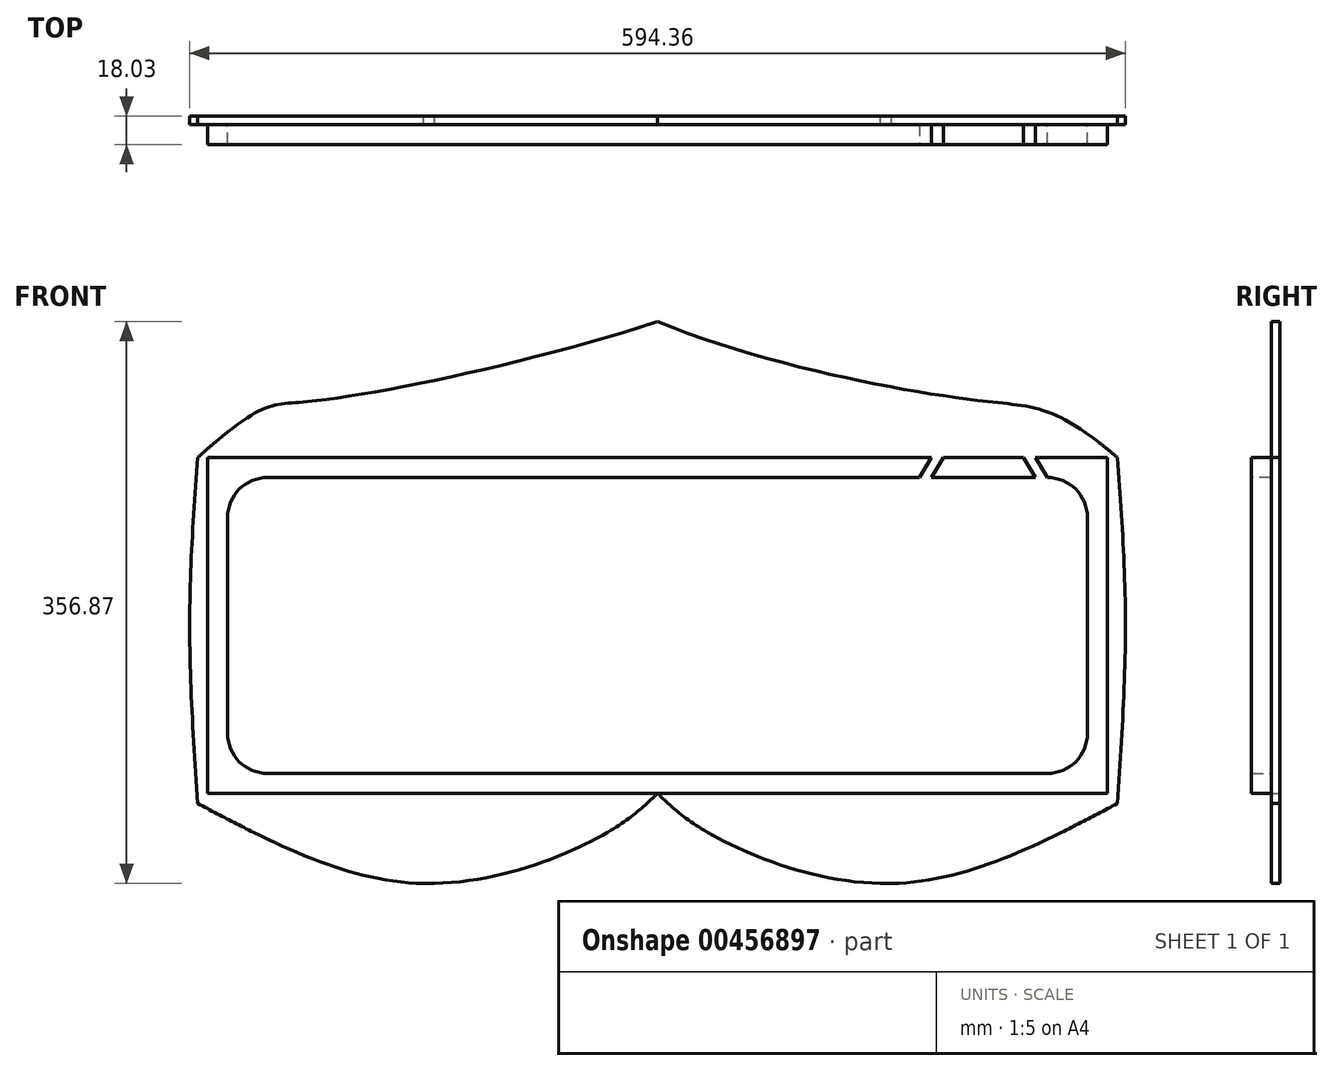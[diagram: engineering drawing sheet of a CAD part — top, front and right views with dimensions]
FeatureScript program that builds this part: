
annotation { "Feature Type Name" : "Feature", "Feature Type Description" : "" }
export const myFeature = defineFeature(function(context is Context, id is Id, definition is map)
    precondition{}
    {
        {
            var Q0;
            Q0=qCreatedBy(makeId("Front.planeOp"),FACE);
            var sketch = newSketch(context, id + "F0", { "sketchPlane" : qUnion([Q0])});
            skLineSegment(sketch, "E0.bottom", {"start": v(0, 0) * mm, "end": v(-584.2, 0) * mm});
            skLineSegment(sketch, "E0.top", {"start": v(0, 219.7) * mm, "end": v(-584.2, 219.7) * mm});
            skLineSegment(sketch, "E0.left", {"start": v(0, 0) * mm, "end": v(0, 219.7) * mm});
            skLineSegment(sketch, "E0.right", {"start": v(-584.2, 0) * mm, "end": v(-584.2, 219.7) * mm});
            skPoint(sketch, "E1", {"position": v(-292.1, 219.7) * mm});
            skSolve(sketch);
        }
        {
            var Q0;
            Q0=makeQuery(id+"F0.imprint","IMPRINT",FACE,{"disambiguationData":[TD([[makeQuery(id+"F0.imprint","IMPRINT",EDGE,{"derivedFrom":sQuery(id+"F0.wireOp",EDGE,"E0.bottom")}),-1.0]])]});
            extrude(context, id + "F1", {"entities" : qUnion([Q0]), "depth" : 5.33 * mm});
        }
        {
            var Q0;
            Q0=makeQuery(id+"F1.opExtrude","CAP_FACE",FACE,{"disambiguationData":[OSD([sQuery(id+"F0.wireOp",EDGE,"E0.bottom"),sQuery(id+"F0.wireOp",EDGE,"E0.top"),sQuery(id+"F0.wireOp",EDGE,"E0.left"),sQuery(id+"F0.wireOp",EDGE,"E0.right")])],"isStart":false});
            var sketch = newSketch(context, id + "F2", { "sketchPlane" : qUnion([Q0])});
            skLineSegment(sketch, "E2", {"start": v(-577.85, 219.7) * mm, "end": v(-577.85, 6.35) * mm});
            skLineSegment(sketch, "E3", {"start": v(-577.85, 6.35) * mm, "end": v(-6.35, 6.35) * mm});
            skLineSegment(sketch, "E4", {"start": v(-6.35, 6.35) * mm, "end": v(-6.35, 219.71) * mm});
            skLineSegment(sketch, "E5", {"start": v(-6.35, 219.71) * mm, "end": v(-577.85, 219.7) * mm});
            skLineSegment(sketch, "E6", {"start": v(-565.15, 207) * mm, "end": v(-565.15, 19.05) * mm});
            skLineSegment(sketch, "E7", {"start": v(-565.15, 19.05) * mm, "end": v(-19.05, 19.05) * mm});
            skLineSegment(sketch, "E8", {"start": v(-19.05, 19.05) * mm, "end": v(-19.05, 207.01) * mm});
            skLineSegment(sketch, "E9", {"start": v(-19.05, 207.01) * mm, "end": v(-565.15, 207) * mm});
            skSolve(sketch);
        }
        {
            var Q0;
            Q0=makeQuery(id+"F2.imprint","IMPRINT",FACE,{"disambiguationData":[TD([[makeQuery(id+"F2.imprint","IMPRINT",EDGE,{"derivedFrom":sQuery(id+"F2.wireOp",EDGE,"E2")}),1.0]])]});
            extrude(context, id + "F3", {"entities" : qUnion([Q0]), "operationType" : NewBodyOperationType.ADD, "depth" : 12.7 * mm});
        }
        {
            var Q0;
            Q0=makeQuery(id+"F3.opExtrude","SWEPT_EDGE",EDGE,{"disambiguationData":[OSD([sQuery(id+"F2.wireOp",EDGE,"E6"),sQuery(id+"F2.wireOp",EDGE,"E9")])]});
            var Q1;
            Q1=makeQuery(id+"F3.opExtrude","SWEPT_EDGE",EDGE,{"disambiguationData":[OSD([sQuery(id+"F2.wireOp",EDGE,"E8"),sQuery(id+"F2.wireOp",EDGE,"E9")])]});
            var Q2;
            Q2=makeQuery(id+"F3.opExtrude","SWEPT_EDGE",EDGE,{"disambiguationData":[OSD([sQuery(id+"F2.wireOp",EDGE,"E7"),sQuery(id+"F2.wireOp",EDGE,"E8")])]});
            var Q3;
            Q3=makeQuery(id+"F3.opExtrude","SWEPT_EDGE",EDGE,{"disambiguationData":[OSD([sQuery(id+"F2.wireOp",EDGE,"E6"),sQuery(id+"F2.wireOp",EDGE,"E7")])]});
            fillet(context, id + "F4", {"entities" : qUnion([Q0, Q1, Q2, Q3]), "radius" : 25.4 * mm, "tangentPropagation" : true, "allowEdgeOverflow" : false});
        }
        {
            var Q0;
            Q0=makeQuery(id+"F3.opExtrude","CAP_FACE",FACE,{"disambiguationData":[OSD([sQuery(id+"F2.wireOp",EDGE,"E2"),sQuery(id+"F2.wireOp",EDGE,"E3"),sQuery(id+"F2.wireOp",EDGE,"E4"),sQuery(id+"F2.wireOp",EDGE,"E5"),sQuery(id+"F2.wireOp",EDGE,"E6"),sQuery(id+"F2.wireOp",EDGE,"E7"),sQuery(id+"F2.wireOp",EDGE,"E8"),sQuery(id+"F2.wireOp",EDGE,"E9")])],"isStart":false});
            var sketch = newSketch(context, id + "F5", { "sketchPlane" : qUnion([Q0])});
            skPoint(sketch, "E10", {"position": v(-118.11, 219.7) * mm});
            skPoint(sketch, "E11", {"position": v(-110.5, 219.7) * mm});
            skPoint(sketch, "E12", {"position": v(-59.69, 219.7) * mm});
            skPoint(sketch, "E13", {"position": v(-52.07, 219.7) * mm});
            skPoint(sketch, "E14", {"position": v(-376.28, 272.75) * mm});
            skPoint(sketch, "E15", {"position": v(-12.7, 0) * mm});
            skPoint(sketch, "E16", {"position": v(-20.32, 0) * mm});
            skLineSegment(sketch, "E17", {"start": v(-20.32, 0) * mm, "end": v(-12.7, 0) * mm});
            skPoint(sketch, "E18", {"position": v(-118.11, 207.01) * mm});
            skPoint(sketch, "E19", {"position": v(-125.73, 207.01) * mm});
            skLineSegment(sketch, "E20", {"start": v(-125.73, 207.01) * mm, "end": v(-118.11, 219.7) * mm});
            skLineSegment(sketch, "E21", {"start": v(-125.73, 207.01) * mm, "end": v(-118.11, 207.01) * mm});
            skLineSegment(sketch, "E22", {"start": v(-118.11, 207.01) * mm, "end": v(-110.5, 219.7) * mm});
            skLineSegment(sketch, "E23", {"start": v(-118.11, 219.7) * mm, "end": v(-110.5, 219.7) * mm});
            skLineSegment(sketch, "E24", {"start": v(-59.69, 219.7) * mm, "end": v(-52.07, 219.7) * mm});
            skLineSegment(sketch, "E25", {"start": v(-110.5, 219.7) * mm, "end": v(-59.69, 219.7) * mm});
            skLineSegment(sketch, "E26", {"start": v(-59.69, 219.7) * mm, "end": v(-110.5, 219.7) * mm});
            skLineSegment(sketch, "E27", {"start": v(-110.5, 219.7) * mm, "end": v(-113.58, 214.56) * mm});
            skPoint(sketch, "E28", {"position": v(-44.45, 207.01) * mm});
            skPoint(sketch, "E29", {"position": v(-52.07, 207.01) * mm});
            skLineSegment(sketch, "E30", {"start": v(-59.69, 219.7) * mm, "end": v(-52.07, 207.01) * mm});
            skLineSegment(sketch, "E31", {"start": v(-52.07, 219.7) * mm, "end": v(-44.45, 207.01) * mm});
            skLineSegment(sketch, "E32", {"start": v(-52.07, 207.01) * mm, "end": v(-44.45, 207.01) * mm});
            skLineSegment(sketch, "E33", {"start": v(-52.07, 219.7) * mm, "end": v(-59.69, 219.7) * mm});
            skPoint(sketch, "E34", {"position": v(-56.6, 214.56) * mm});
            skLineSegment(sketch, "E35", {"start": v(-113.58, 214.56) * mm, "end": v(-56.6, 214.56) * mm});
            skSolve(sketch);
        }
        {
            var Q0;
            Q0=makeQuery(id+"F5.imprint","IMPRINT",FACE,{"disambiguationData":[TD([[makeQuery(id+"F5.imprint","IMPRINT",EDGE,{"derivedFrom":sQuery(id+"F5.wireOp",EDGE,"E20")}),-1.0]])]});
            var Q1;
            {var subQ8=sQuery(id+"F5.wireOp",EDGE,"RZINdJYM-ykuw-GilU-JIjt-DnibDYUsXZuo");Q1=makeQuery(id+"F5.imprint","IMPRINT",FACE,{"disambiguationData":[TD([[makeQuery(id+"F5.imprint","IMPRINT",EDGE,{"derivedFrom":subQ8}),1.0]])]});}
            var Q2;
            Q2=makeQuery(id+"F5.imprint","IMPRINT",FACE,{"disambiguationData":[TD([[makeQuery(id+"F5.imprint","IMPRINT",EDGE,{"derivedFrom":sQuery(id+"F5.wireOp",EDGE,"RZINdJYM-ykuw-GilU-JIjt-DnibDYUsXZuo")}),-1.0]])]});
            var Q3;
            Q3=makeQuery(id+"F5.imprint","IMPRINT",FACE,{"disambiguationData":[TD([[makeQuery(id+"F5.imprint","IMPRINT",EDGE,{"derivedFrom":sQuery(id+"F5.wireOp",EDGE,"NQJIxGkc-Vixr-o2zM-VUe3-bVQ5EoZFKsab")}),1.0]])]});
            var Q4;
            Q4=makeQuery(id+"F5.imprint","IMPRINT",FACE,{"disambiguationData":[TD([[makeQuery(id+"F5.imprint","IMPRINT",EDGE,{"derivedFrom":sQuery(id+"F5.wireOp",EDGE,"E30")}),1.0]])]});
            var Q5;
            {var subQ0=sQuery(id+"F5.wireOp",EDGE,"E26");Q5=makeQuery(id+"F5.imprint","IMPRINT",FACE,{"disambiguationData":[TD([[makeQuery(id+"F5.imprint","IMPRINT",EDGE,{"derivedFrom":subQ0}),1.0]])]});}
            extrude(context, id + "F6", {"entities" : qUnion([Q0, Q1, Q2, Q3, Q4, Q5]), "operationType" : NewBodyOperationType.REMOVE, "oppositeDirection" : true, "depth" : 12.7 * mm});
        }
        {
            var Q0;
            Q0=makeQuery(id+"F1.opExtrude","CAP_FACE",FACE,{"disambiguationData":[OSD([sQuery(id+"F0.wireOp",EDGE,"E0.bottom"),sQuery(id+"F0.wireOp",EDGE,"E0.top"),sQuery(id+"F0.wireOp",EDGE,"E0.left"),sQuery(id+"F0.wireOp",EDGE,"E0.right")])],"isStart":true});
            var sketch = newSketch(context, id + "F7", { "sketchPlane" : qUnion([Q0])});
            skLineSegment(sketch, "E36", {"start": v(0, 0) * mm, "end": v(-5.08, 0) * mm});
            skLineSegment(sketch, "E37", {"start": v(-5.08, 0) * mm, "end": v(-5.08, 229.87) * mm});
            skLineSegment(sketch, "E38", {"start": v(-5.08, 229.87) * mm, "end": v(589.28, 229.87) * mm});
            skLineSegment(sketch, "E39", {"start": v(589.28, 229.87) * mm, "end": v(589.28, 0) * mm});
            skLineSegment(sketch, "E40", {"start": v(589.28, 0) * mm, "end": v(584.2, 0) * mm});
            skPoint(sketch, "E41", {"position": v(589.28, 114.93) * mm});
            skPoint(sketch, "E42", {"position": v(584.2, 109.85) * mm});
            skPoint(sketch, "E43", {"position": v(292.1, 229.87) * mm});
            skPoint(sketch, "E44", {"position": v(292.1, 219.7) * mm});
            skPoint(sketch, "E45", {"position": v(-5.08, 114.93) * mm});
            skPoint(sketch, "E46", {"position": v(0, 109.85) * mm});
            skPoint(sketch, "E47", {"position": v(538.48, 229.87) * mm});
            skPoint(sketch, "E48", {"position": v(45.72, 229.87) * mm});
            skPoint(sketch, "E49", {"position": v(-5.08, 191.77) * mm});
            skPoint(sketch, "E50", {"position": v(589.28, 191.77) * mm});
            skPoint(sketch, "E51", {"position": v(584.2, 183.25) * mm});
            skPoint(sketch, "E52", {"position": v(0, 176.13) * mm});
            skPoint(sketch, "E53", {"position": v(589.28, 63.5) * mm});
            skPoint(sketch, "E54", {"position": v(-5.08, 63.5) * mm});
            skPoint(sketch, "E55", {"position": v(0, 219.7) * mm});
            skPoint(sketch, "E56", {"position": v(584.2, 219.7) * mm});
            skPoint(sketch, "E57", {"position": v(393.7, 219.7) * mm});
            skPoint(sketch, "E58", {"position": v(190.5, 219.7) * mm});
            skLineSegment(sketch, "E59", {"start": v(292.1, 219.7) * mm, "end": v(-5.08, 229.87) * mm});
            skLineSegment(sketch, "E60", {"start": v(292.1, 219.7) * mm, "end": v(589.28, 229.87) * mm});
            skLineSegment(sketch, "E61", {"start": v(589.28, -18.42) * mm, "end": v(-5.08, -18.42) * mm});
            skLineSegment(sketch, "E62", {"start": v(589.28, 0) * mm, "end": v(589.28, -18.42) * mm});
            skLineSegment(sketch, "E63", {"start": v(292.1, 229.87) * mm, "end": v(292.1, 306.07) * mm});
            skPoint(sketch, "E64", {"position": v(292.1, -18.42) * mm});
            skLineSegment(sketch, "E65", {"start": v(589.28, -18.42) * mm, "end": v(589.28, -50.8) * mm});
            skLineSegment(sketch, "E66", {"start": v(589.28, -50.8) * mm, "end": v(292.1, -50.8) * mm});
            skPoint(sketch, "E67", {"position": v(292.1, 0) * mm});
            skPoint(sketch, "E68", {"position": v(440.69, -50.8) * mm});
            skLineSegment(sketch, "E69", {"start": v(292.1, -50.8) * mm, "end": v(-4.91, -50.8) * mm});
            skLineSegment(sketch, "E70", {"start": v(-4.91, -50.8) * mm, "end": v(-5.08, -18.42) * mm});
            skPoint(sketch, "E71", {"position": v(143.6, -50.8) * mm});
            skPoint(sketch, "E72", {"position": v(551.18, -18.42) * mm});
            skPoint(sketch, "E73", {"position": v(33.02, -18.42) * mm});
            skPoint(sketch, "E74", {"position": v(6.35, 219.7) * mm});
            skPoint(sketch, "E75", {"position": v(577.85, 219.7) * mm});
            skPoint(sketch, "E76", {"position": v(6.35, 0) * mm});
            skPoint(sketch, "E77", {"position": v(577.85, 0) * mm});
            skPoint(sketch, "E78", {"position": v(82.55, 229.87) * mm});
            skPoint(sketch, "E79", {"position": v(514.35, 229.87) * mm});
            skLineSegment(sketch, "E80", {"start": v(82.55, 229.87) * mm, "end": v(82.55, 255.27) * mm});
            skLineSegment(sketch, "E81", {"start": v(514.35, 229.87) * mm, "end": v(514.35, 255.27) * mm});
            skLineSegment(sketch, "E82", {"start": v(292.1, 0) * mm, "end": v(292.1, 6.35) * mm});
            skPoint(sketch, "E83", {"position": v(323.85, -18.42) * mm});
            skPoint(sketch, "E84", {"position": v(260.35, -18.42) * mm});
            skFitSpline(sketch, "E85", {"points": [v(292.1, 6.35) * mm, v(323.85, -18.42) * mm, v(440.69, -50.8) * mm, v(584.2, 0) * mm], "startDerivative": vector(117.09, -111.78) * mm, "endDerivative": vector(338.96, 179.53) * mm});
            skFitSpline(sketch, "E86", {"points": [v(584.2, 0) * mm, v(589.28, 114.94) * mm, v(584.2, 219.7) * mm], "startDerivative": vector(15.13, 227.29) * mm, "endDerivative": vector(-15.37, 212.01) * mm});
            skFitSpline(sketch, "E87", {"points": [v(0, 0) * mm, v(-5.08, 114.94) * mm, v(0, 219.7) * mm], "startDerivative": vector(-15.13, 227.29) * mm, "endDerivative": vector(15.37, 212.01) * mm});
            skFitSpline(sketch, "E88", {"points": [v(292.1, 6.35) * mm, v(260.35, -18.42) * mm, v(143.6, -50.8) * mm, v(0, 0) * mm], "startDerivative": vector(-117.11, -111.77) * mm, "endDerivative": vector(-339.14, 179.5) * mm});
            skFitSpline(sketch, "E89", {"points": [v(292.1, 306.07) * mm, v(514.35, 255.27) * mm, v(584.2, 219.7) * mm], "startDerivative": vector(389.1, -127.04) * mm, "endDerivative": vector(333.85, -297.61) * mm});
            skFitSpline(sketch, "E90", {"points": [v(292.1, 306.07) * mm, v(82.55, 255.27) * mm, v(0, 219.7) * mm], "startDerivative": vector(-362.71, -146.77) * mm, "endDerivative": vector(-299.5, -254.41) * mm});
            skSolve(sketch);
        }
        {
            var Q0;
            {var subQ0=sQuery(id+"F7.wireOp",EDGE,"E82");Q0=makeQuery(id+"F7.imprint","IMPRINT",FACE,{"disambiguationData":[TD([[makeQuery(id+"F7.imprint","IMPRINT",EDGE,{"derivedFrom":subQ0}),1.0]])]});}
            var Q1;
            {var subQ0=sQuery(id+"F7.wireOp",EDGE,"E82");Q1=makeQuery(id+"F7.imprint","IMPRINT",FACE,{"disambiguationData":[TD([[makeQuery(id+"F7.imprint","IMPRINT",EDGE,{"derivedFrom":subQ0}),-1.0]])]});}
            extrude(context, id + "F8", {"entities" : qUnion([Q0, Q1]), "operationType" : NewBodyOperationType.REMOVE, "depth" : -5.33 * mm});
        }
        {
            var Q0;
            {var subQ0=sQuery(id+"F7.wireOp",EDGE,"E80");Q0=makeQuery(id+"F7.imprint","IMPRINT",FACE,{"disambiguationData":[TD([[makeQuery(id+"F7.imprint","IMPRINT",EDGE,{"derivedFrom":subQ0}),1.0]])]});}
            var Q1;
            {var subQ0=sQuery(id+"F7.wireOp",EDGE,"E63");Q1=makeQuery(id+"F7.imprint","IMPRINT",FACE,{"disambiguationData":[TD([[makeQuery(id+"F7.imprint","IMPRINT",EDGE,{"derivedFrom":subQ0}),1.0]])]});}
            var Q2;
            {var subQ0=sQuery(id+"F7.wireOp",EDGE,"E63");Q2=makeQuery(id+"F7.imprint","IMPRINT",FACE,{"disambiguationData":[TD([[makeQuery(id+"F7.imprint","IMPRINT",EDGE,{"derivedFrom":subQ0}),-1.0]])]});}
            var Q3;
            {var subQ0=sQuery(id+"F7.wireOp",EDGE,"E81");Q3=makeQuery(id+"F7.imprint","IMPRINT",FACE,{"disambiguationData":[TD([[makeQuery(id+"F7.imprint","IMPRINT",EDGE,{"derivedFrom":subQ0}),-1.0]])]});}
            var Q4;
            {var subQ0=sQuery(id+"F7.wireOp",EDGE,"E60");var subQ3=sQuery(id+"F7.wireOp",EDGE,"c924a81b-7c33-454b-bec7-e8dcdf9a45a6");var subQ4=makeQuery(id+"F7.imprint","INTERSECT",VERTEX,{"derivedFrom":[subQ0,subQ3]});Q4=makeQuery(id+"F7.imprint","IMPRINT",FACE,{"disambiguationData":[TD([[makeQuery(id+"F7.imprint","IMPRINT",EDGE,{"disambiguationData":[TD([[subQ4,1.0]])],"derivedFrom":subQ0}),-1.0]])]});}
            var Q5;
            {var subQ0=sQuery(id+"F7.wireOp",EDGE,"E38");var subQ7=makeQuery(id+"F7.imprint","INTERSECT",VERTEX,{"derivedFrom":[subQ0,sQuery(id+"F7.wireOp",EDGE,"E80")]});Q5=makeQuery(id+"F7.imprint","IMPRINT",FACE,{"disambiguationData":[TD([[makeQuery(id+"F7.imprint","IMPRINT",EDGE,{"disambiguationData":[TD([[subQ7,1.0]])],"derivedFrom":subQ0}),-1.0]])]});}
            var Q6;
            {var subQ0=sQuery(id+"F7.wireOp",EDGE,"E59");var subQ3=sQuery(id+"F7.wireOp",EDGE,"3c0d3bf1-8729-4a13-bacb-ae9455c1fce2");var subQ4=makeQuery(id+"F7.imprint","INTERSECT",VERTEX,{"derivedFrom":[subQ0,subQ3]});Q6=makeQuery(id+"F7.imprint","IMPRINT",FACE,{"disambiguationData":[TD([[makeQuery(id+"F7.imprint","IMPRINT",EDGE,{"disambiguationData":[TD([[subQ4,1.0]])],"derivedFrom":subQ0}),1.0]])]});}
            var Q7;
            {var subQ0=sQuery(id+"F7.wireOp",EDGE,"c8baf287-04a5-4912-9b82-47411f5b9158");var subQ1=sQuery(id+"F7.wireOp",EDGE,"E61");var subQ2=makeQuery(id+"F7.imprint","INTERSECT",VERTEX,{"disambiguationData":[OD(0.0)],"derivedFrom":[subQ1,subQ0]});Q7=makeQuery(id+"F7.imprint","IMPRINT",FACE,{"disambiguationData":[TD([[makeQuery(id+"F7.imprint","IMPRINT",EDGE,{"disambiguationData":[TD([[subQ2,1.0]])],"derivedFrom":subQ1}),-1.0]])]});}
            var Q8;
            {var subQ0=sQuery(id+"F7.wireOp",EDGE,"c8baf287-04a5-4912-9b82-47411f5b9158");var subQ1=sQuery(id+"F7.wireOp",EDGE,"E61");var subQ2=makeQuery(id+"F7.imprint","INTERSECT",VERTEX,{"disambiguationData":[OD(0.0)],"derivedFrom":[subQ1,subQ0]});Q8=makeQuery(id+"F7.imprint","IMPRINT",FACE,{"disambiguationData":[TD([[makeQuery(id+"F7.imprint","IMPRINT",EDGE,{"disambiguationData":[TD([[subQ2,1.0]])],"derivedFrom":subQ1}),1.0]])]});}
            var Q9;
            {var subQ0=sQuery(id+"F7.wireOp",EDGE,"c47f91c2-344f-4819-b83d-0fa72e82eadb");var subQ1=sQuery(id+"F7.wireOp",EDGE,"E61");var subQ2=makeQuery(id+"F7.imprint","INTERSECT",VERTEX,{"disambiguationData":[OD(0.0)],"derivedFrom":[subQ1,subQ0]});Q9=makeQuery(id+"F7.imprint","IMPRINT",FACE,{"disambiguationData":[TD([[makeQuery(id+"F7.imprint","IMPRINT",EDGE,{"disambiguationData":[TD([[subQ2,-1.0]])],"derivedFrom":subQ1}),-1.0]])]});}
            var Q10;
            {var subQ0=sQuery(id+"F7.wireOp",EDGE,"c47f91c2-344f-4819-b83d-0fa72e82eadb");var subQ1=sQuery(id+"F7.wireOp",EDGE,"E61");var subQ2=makeQuery(id+"F7.imprint","INTERSECT",VERTEX,{"disambiguationData":[OD(0.0)],"derivedFrom":[subQ1,subQ0]});Q10=makeQuery(id+"F7.imprint","IMPRINT",FACE,{"disambiguationData":[TD([[makeQuery(id+"F7.imprint","IMPRINT",EDGE,{"disambiguationData":[TD([[subQ2,-1.0]])],"derivedFrom":subQ1}),1.0]])]});}
            var Q11;
            {var subQ0=sQuery(id+"F7.wireOp",EDGE,"E85");var subQ1=sQuery(id+"F7.wireOp",EDGE,"E61");var subQ2=makeQuery(id+"F7.imprint","INTERSECT",VERTEX,{"disambiguationData":[OD(0.0)],"derivedFrom":[subQ1,subQ0]});Q11=makeQuery(id+"F7.imprint","IMPRINT",FACE,{"disambiguationData":[TD([[makeQuery(id+"F7.imprint","IMPRINT",EDGE,{"disambiguationData":[TD([[subQ2,-1.0]])],"derivedFrom":subQ1}),1.0]])]});}
            var Q12;
            {var subQ0=sQuery(id+"F7.wireOp",EDGE,"E85");var subQ1=sQuery(id+"F7.wireOp",EDGE,"E61");var subQ2=makeQuery(id+"F7.imprint","INTERSECT",VERTEX,{"disambiguationData":[OD(0.0)],"derivedFrom":[subQ1,subQ0]});Q12=makeQuery(id+"F7.imprint","IMPRINT",FACE,{"disambiguationData":[TD([[makeQuery(id+"F7.imprint","IMPRINT",EDGE,{"disambiguationData":[TD([[subQ2,-1.0]])],"derivedFrom":subQ1}),-1.0]])]});}
            var Q13;
            {var subQ0=sQuery(id+"F7.wireOp",EDGE,"E88");var subQ1=sQuery(id+"F7.wireOp",EDGE,"E61");var subQ2=makeQuery(id+"F7.imprint","INTERSECT",VERTEX,{"disambiguationData":[OD(0.0)],"derivedFrom":[subQ1,subQ0]});Q13=makeQuery(id+"F7.imprint","IMPRINT",FACE,{"disambiguationData":[TD([[makeQuery(id+"F7.imprint","IMPRINT",EDGE,{"disambiguationData":[TD([[subQ2,1.0]])],"derivedFrom":subQ1}),1.0]])]});}
            var Q14;
            {var subQ0=sQuery(id+"F7.wireOp",EDGE,"E88");var subQ1=sQuery(id+"F7.wireOp",EDGE,"E61");var subQ2=makeQuery(id+"F7.imprint","INTERSECT",VERTEX,{"disambiguationData":[OD(0.0)],"derivedFrom":[subQ1,subQ0]});Q14=makeQuery(id+"F7.imprint","IMPRINT",FACE,{"disambiguationData":[TD([[makeQuery(id+"F7.imprint","IMPRINT",EDGE,{"disambiguationData":[TD([[subQ2,1.0]])],"derivedFrom":subQ1}),-1.0]])]});}
            var Q15;
            {var subQ4=makeQuery(id+"F1.opExtrude","CAP_EDGE",EDGE,{"disambiguationData":[OSD([sQuery(id+"F0.wireOp",EDGE,"E0.right")])],"isStart":true});Q15=makeQuery(id+"F7.imprint","IMPRINT",FACE,{"disambiguationData":[TD([[makeQuery(id+"F7.imprint","IMPRINT",EDGE,{"derivedFrom":subQ4}),-1.0]])]});}
            var Q16;
            {var subQ4=makeQuery(id+"F1.opExtrude","CAP_EDGE",EDGE,{"disambiguationData":[OSD([sQuery(id+"F0.wireOp",EDGE,"E0.left")])],"isStart":true});Q16=makeQuery(id+"F7.imprint","IMPRINT",FACE,{"disambiguationData":[TD([[makeQuery(id+"F7.imprint","IMPRINT",EDGE,{"derivedFrom":subQ4}),1.0]])]});}
            extrude(context, id + "F9", {"entities" : qUnion([Q0, Q1, Q2, Q3, Q4, Q5, Q6, Q7, Q8, Q9, Q10, Q11, Q12, Q13, Q14, Q15, Q16]), "operationType" : NewBodyOperationType.ADD, "depth" : -5.33 * mm});
        }
    });
